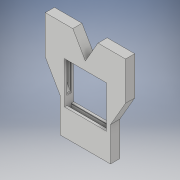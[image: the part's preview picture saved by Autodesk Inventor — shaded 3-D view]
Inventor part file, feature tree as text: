
AUTODESK INVENTOR PART (.ipt)
format: ipt  version: 2017 (Build 210142000, 142)  size: 178,688 bytes
history: native  units: in
note: dims shown in document units (in); Inventor stores cm internally (conversion verified against a paired STEP export)
features: other x4, plane x1, sketch x1
ambient origin geometry x8: Origin, YZ Plane, XZ Plane, XY Plane, X Axis, Y Axis, Z Axis, Center Point
bodies: Solid1 (feature_tree)
feature tree (6):
  other  "end door frame (100).ipt"
  plane  "Work Plane1"
  sketch  "Sketch1"  dims[d0=0.0354in d1=4.5in]
  other  "mate for doors"
  other  "rame of door::end door frame (100).ipt"
  other  "TaggingFeature1"
